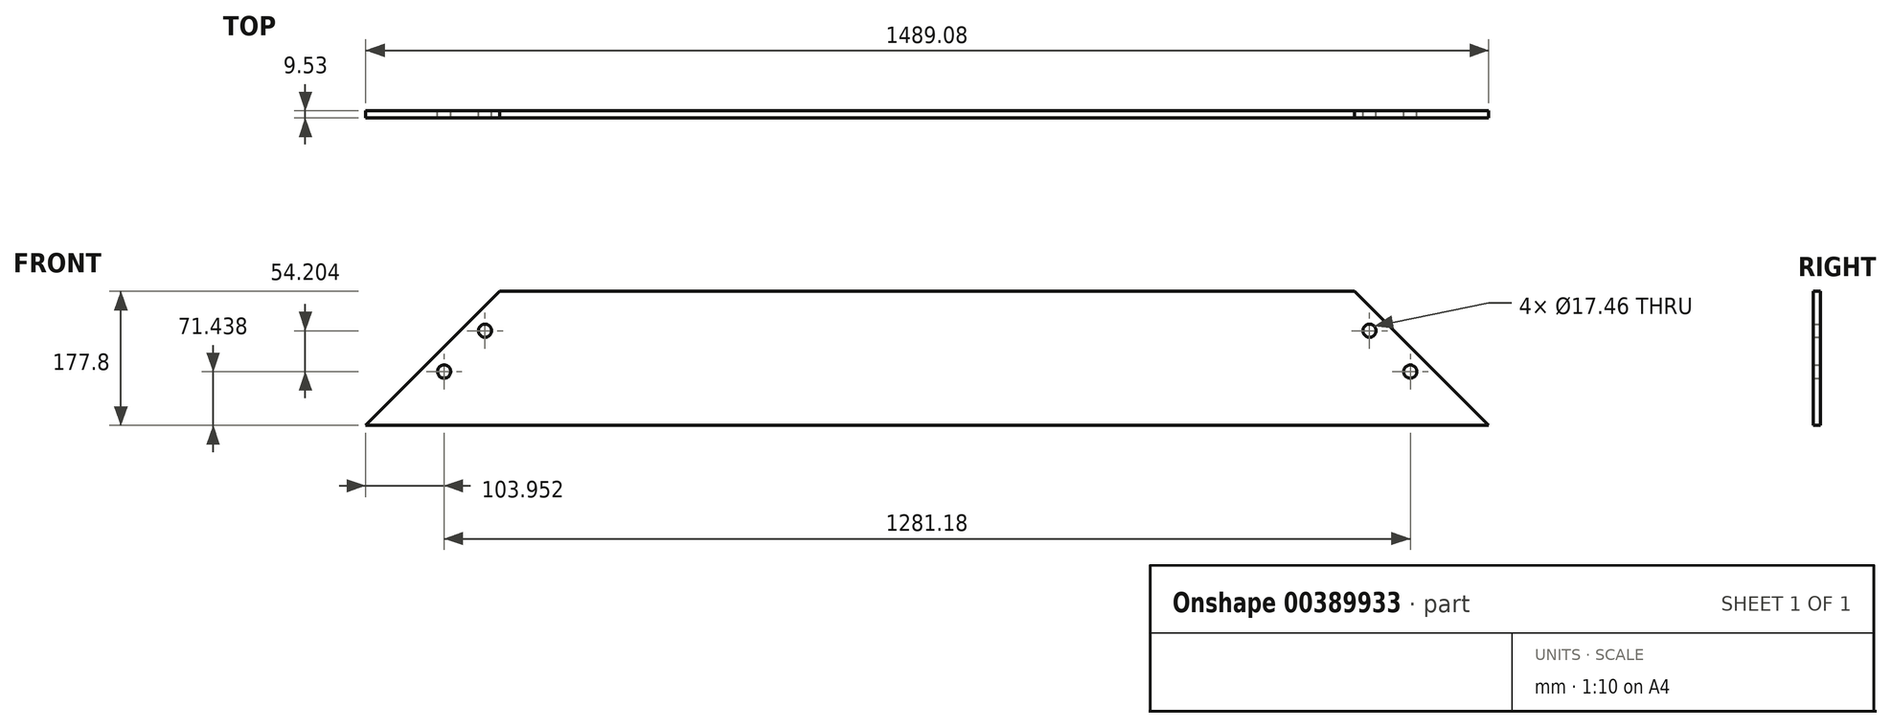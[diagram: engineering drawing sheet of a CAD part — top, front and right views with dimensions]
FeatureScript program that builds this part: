
annotation { "Feature Type Name" : "Feature", "Feature Type Description" : "" }
export const myFeature = defineFeature(function(context is Context, id is Id, definition is map)
    precondition{}
    {
        {
            var Q0;
            Q0=qCreatedBy(makeId("Front.planeOp"),FACE);
            var sketch = newSketch(context, id + "F0", { "sketchPlane" : qUnion([Q0])});
            skLineSegment(sketch, "E0.bottom", {"start": v(744.54, -88.9) * mm, "end": v(-744.54, -88.9) * mm});
            skLineSegment(sketch, "E0.top", {"start": v(566.74, 88.9) * mm, "end": v(-566.74, 88.9) * mm});
            skPoint(sketch, "E0.middle", {"position": v(0, 0) * mm});
            skLineSegment(sketch, "E1", {"start": v(-744.54, -88.9) * mm, "end": v(-566.74, 88.9) * mm});
            skLineSegment(sketch, "E2", {"start": v(744.54, -88.9) * mm, "end": v(566.74, 88.9) * mm});
            skCircle(sketch, "E3", {"center": v(-586.38, 36.74) * mm, "radius": 8.73 * mm});
            skCircle(sketch, "E4", {"center": v(-640.59, -17.46) * mm, "radius": 8.73 * mm});
            skCircle(sketch, "E5.MirrorC", {"center": v(586.38, 36.74) * mm, "radius": 8.73 * mm});
            skCircle(sketch, "E6.MirrorC", {"center": v(640.59, -17.46) * mm, "radius": 8.73 * mm});
            skSolve(sketch);
        }
        {
            var Q0;
            Q0=makeQuery(id+"F0.imprint","IMPRINT",FACE,{"disambiguationData":[TD([[makeQuery(id+"F0.imprint","IMPRINT",EDGE,{"derivedFrom":sQuery(id+"F0.wireOp",EDGE,"E0.bottom")}),-1.0]])]});
            extrude(context, id + "F1", {"entities" : qUnion([Q0]), "depth" : 9.52 * mm});
        }
    });
